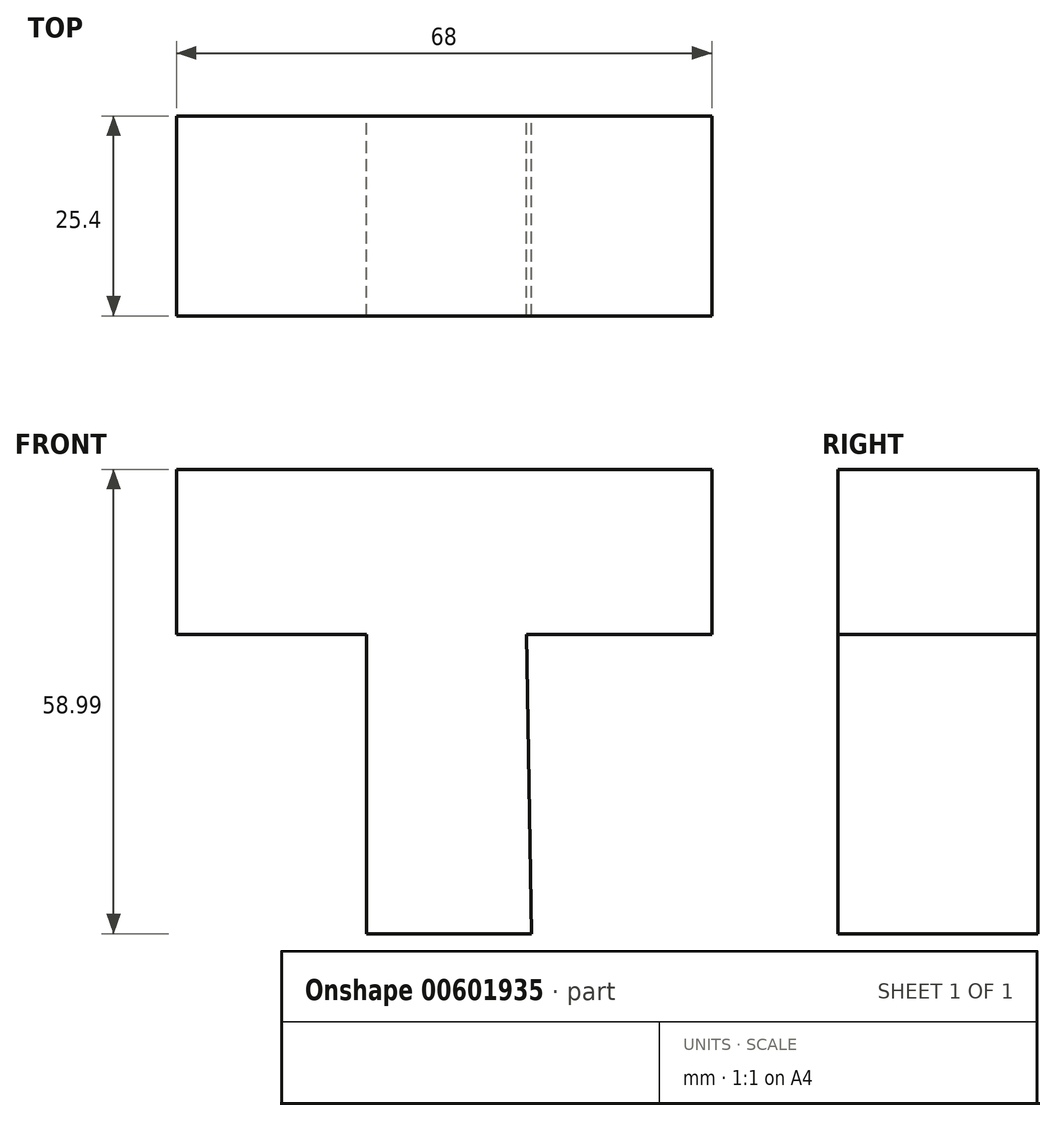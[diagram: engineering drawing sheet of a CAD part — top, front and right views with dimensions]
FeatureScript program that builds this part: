
annotation { "Feature Type Name" : "Feature", "Feature Type Description" : "" }
export const myFeature = defineFeature(function(context is Context, id is Id, definition is map)
    precondition{}
    {
        {
            var Q0;
            Q0=qCreatedBy(makeId("Front.planeOp"),FACE);
            var sketch = newSketch(context, id + "F0", { "sketchPlane" : qUnion([Q0])});
            skLineSegment(sketch, "E0", {"start": v(-33.42, 21) * mm, "end": v(-33.42, 0) * mm});
            skLineSegment(sketch, "E1", {"start": v(-33.42, 21) * mm, "end": v(34.58, 21) * mm});
            skLineSegment(sketch, "E2", {"start": v(34.58, 21) * mm, "end": v(34.58, 0) * mm});
            skLineSegment(sketch, "E3", {"start": v(34.58, 0) * mm, "end": v(11.01, 0) * mm});
            skLineSegment(sketch, "E4", {"start": v(-33.42, 0) * mm, "end": v(-9.3, 0) * mm});
            skLineSegment(sketch, "E5", {"start": v(-9.3, 0) * mm, "end": v(-9.3, -38) * mm});
            skLineSegment(sketch, "E6", {"start": v(-9.3, -38) * mm, "end": v(11.7, -38) * mm});
            skLineSegment(sketch, "E7", {"start": v(11.7, -38) * mm, "end": v(11.01, 0) * mm});
            skSolve(sketch);
        }
        {
            var Q0;
            Q0 = qSketchRegion(id + "F0", true);
            extrude(context, id + "F1", {"entities" : qUnion([Q0]), "depth" : 25.4 * mm, "offsetDistance" : 25.4 * mm});
        }
    });
